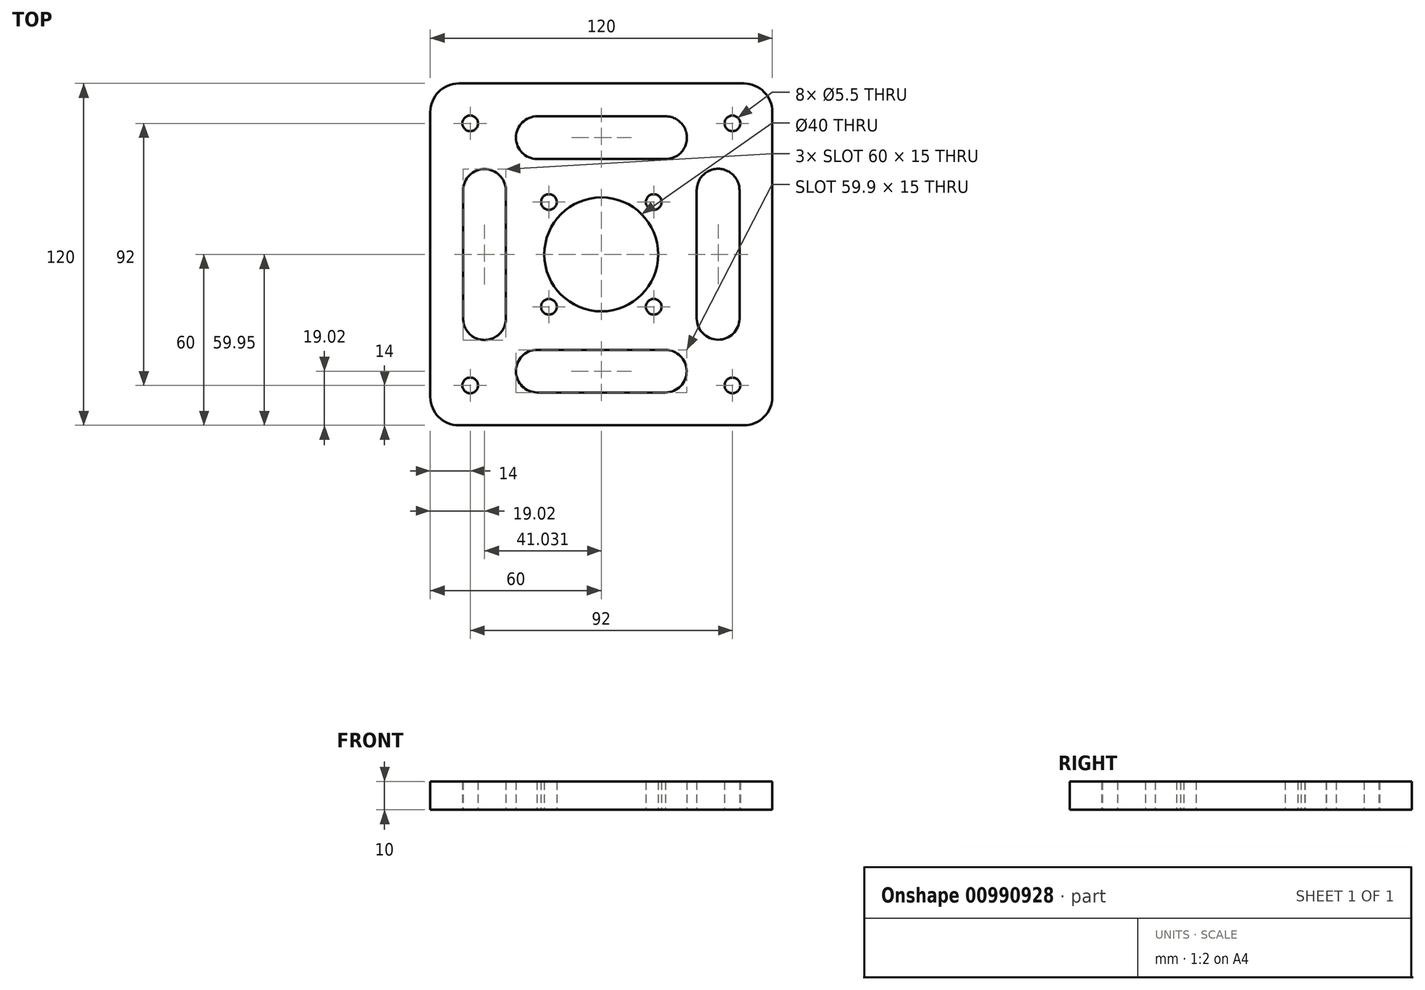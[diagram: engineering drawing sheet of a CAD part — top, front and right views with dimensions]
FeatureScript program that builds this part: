
annotation { "Feature Type Name" : "Feature", "Feature Type Description" : "" }
export const myFeature = defineFeature(function(context is Context, id is Id, definition is map)
    precondition{}
    {
        {
            var Q0;
            Q0=qCreatedBy(makeId("Top.planeOp"),FACE);
            var sketch = newSketch(context, id + "F0", { "sketchPlane" : qUnion([Q0])});
            skLineSegment(sketch, "E0.bottom", {"start": v(50, -60) * mm, "end": v(-50, -60) * mm});
            skLineSegment(sketch, "E0.top", {"start": v(50, 60) * mm, "end": v(-50, 60) * mm});
            skLineSegment(sketch, "E0.left", {"start": v(60, -50) * mm, "end": v(60, 50) * mm});
            skLineSegment(sketch, "E0.right", {"start": v(-60, -50) * mm, "end": v(-60, 50) * mm});
            skPoint(sketch, "E0.middle", {"position": v(0, 0) * mm});
            skCircle(sketch, "E1", {"center": v(0, 0) * mm, "radius": 20 * mm});
            skLineSegment(sketch, "E2", {"start": v(20, 0) * mm, "end": v(60, 0) * mm, "construction": true});
            skLineSegment(sketch, "E3", {"start": v(0, -20) * mm, "end": v(0, -60) * mm, "construction": true});
            skCircle(sketch, "E4", {"center": v(-46, 46) * mm, "radius": 2.75 * mm});
            skCircle(sketch, "E5.MirrorC", {"center": v(46, 46) * mm, "radius": 2.75 * mm});
            skCircle(sketch, "E6.MirrorC", {"center": v(-46, -46) * mm, "radius": 2.75 * mm});
            skCircle(sketch, "E7.MirrorC", {"center": v(46, -46) * mm, "radius": 2.75 * mm});
            skCircle(sketch, "E8", {"center": v(-18.38, 18.38) * mm, "radius": 2.75 * mm});
            skCircle(sketch, "E9.MirrorC", {"center": v(18.38, 18.38) * mm, "radius": 2.75 * mm});
            skCircle(sketch, "E10.MirrorC", {"center": v(-18.38, -18.38) * mm, "radius": 2.75 * mm});
            skCircle(sketch, "E11.MirrorC", {"center": v(18.38, -18.38) * mm, "radius": 2.75 * mm});
            skCircle(sketch, "E12", {"center": v(0, 0) * mm, "radius": 26 * mm, "construction": true});
            skLineSegment(sketch, "E13.left", {"start": v(-33.48, -22.45) * mm, "end": v(-33.48, 22.55) * mm});
            skLineSegment(sketch, "E13.right", {"start": v(-48.48, -22.55) * mm, "end": v(-48.48, 22.45) * mm});
            skPoint(sketch, "E13.middle", {"position": v(-40.98, 0) * mm});
            skLineSegment(sketch, "E14.MirrorCS", {"start": v(48.48, -22.55) * mm, "end": v(48.48, 22.45) * mm});
            skLineSegment(sketch, "E15.MirrorCS", {"start": v(33.48, -22.45) * mm, "end": v(33.48, 22.55) * mm});
            skLineSegment(sketch, "E16", {"start": v(-60, 60) * mm, "end": v(60, -60) * mm, "construction": true});
            skLineSegment(sketch, "E17.MirrorCS", {"start": v(22.45, -33.48) * mm, "end": v(-22.55, -33.48) * mm});
            skLineSegment(sketch, "E18.MirrorCS", {"start": v(22.55, -48.48) * mm, "end": v(-22.45, -48.48) * mm});
            skLineSegment(sketch, "E19.MirrorCS", {"start": v(22.45, 33.48) * mm, "end": v(-22.55, 33.48) * mm});
            skLineSegment(sketch, "E20.MirrorCS", {"start": v(22.55, 48.48) * mm, "end": v(-22.45, 48.48) * mm});
            skPoint(sketch, "E21.visualSharp", {"position": v(-60, 60) * mm});
            skArc(sketch, "E21.filletArc", {"start": v(-50, 60) * mm, "mid": v(-57.07, 57.07) * mm, "end": v(-60, 50) * mm});
            skPoint(sketch, "E22.visualSharp", {"position": v(60, 60) * mm});
            skArc(sketch, "E22.filletArc", {"start": v(60, 50) * mm, "mid": v(57.07, 57.07) * mm, "end": v(50, 60) * mm});
            skPoint(sketch, "E23.visualSharp", {"position": v(-60, -60) * mm});
            skArc(sketch, "E23.filletArc", {"start": v(-60, -50) * mm, "mid": v(-57.07, -57.07) * mm, "end": v(-50, -60) * mm});
            skPoint(sketch, "E24.visualSharp", {"position": v(60, -60) * mm});
            skArc(sketch, "E24.filletArc", {"start": v(50, -60) * mm, "mid": v(57.07, -57.07) * mm, "end": v(60, -50) * mm});
            skArc(sketch, "E25", {"start": v(-33.48, 22.55) * mm, "mid": v(-41.03, 29.95) * mm, "end": v(-48.48, 22.45) * mm});
            skArc(sketch, "E26", {"start": v(-48.48, -22.55) * mm, "mid": v(-40.93, -30.05) * mm, "end": v(-33.48, -22.45) * mm});
            skArc(sketch, "E27", {"start": v(-22.55, -33.48) * mm, "mid": v(-29.95, -41.03) * mm, "end": v(-22.45, -48.48) * mm});
            skArc(sketch, "E28", {"start": v(22.55, -48.48) * mm, "mid": v(29.95, -40.93) * mm, "end": v(22.45, -33.48) * mm});
            skArc(sketch, "E29", {"start": v(33.48, -22.45) * mm, "mid": v(40.93, -29.95) * mm, "end": v(48.48, -22.55) * mm});
            skArc(sketch, "E30", {"start": v(48.48, 22.45) * mm, "mid": v(41.03, 30.05) * mm, "end": v(33.48, 22.55) * mm});
            skArc(sketch, "E31", {"start": v(22.45, 33.48) * mm, "mid": v(30.05, 40.93) * mm, "end": v(22.55, 48.48) * mm});
            skArc(sketch, "E32", {"start": v(-22.45, 48.48) * mm, "mid": v(-29.95, 41.03) * mm, "end": v(-22.55, 33.48) * mm});
            skPoint(sketch, "E33.orphan", {"position": v(-22.55, -33.48) * mm});
            skPoint(sketch, "E34.orphan", {"position": v(22.45, -33.48) * mm});
            skPoint(sketch, "E35.orphan", {"position": v(48.48, -22.55) * mm});
            skPoint(sketch, "E36.MirrorCS.start.orphan", {"position": v(33.48, -22.45) * mm});
            skPoint(sketch, "E37.orphan", {"position": v(22.55, 48.48) * mm});
            skPoint(sketch, "E38.MirrorCS.start.orphan", {"position": v(22.45, 33.48) * mm});
            skPoint(sketch, "E39.orphan", {"position": v(-22.45, 48.48) * mm});
            skPoint(sketch, "E40.MirrorCS.start.orphan", {"position": v(-22.55, 33.48) * mm});
            skSolve(sketch);
        }
        {
            var Q0;
            Q0 = qSketchRegion(id + "F0", true);
            extrude(context, id + "F1", {"entities" : qUnion([Q0]), "depth" : 10 * mm, "offsetDistance" : 25 * mm});
        }
    });
